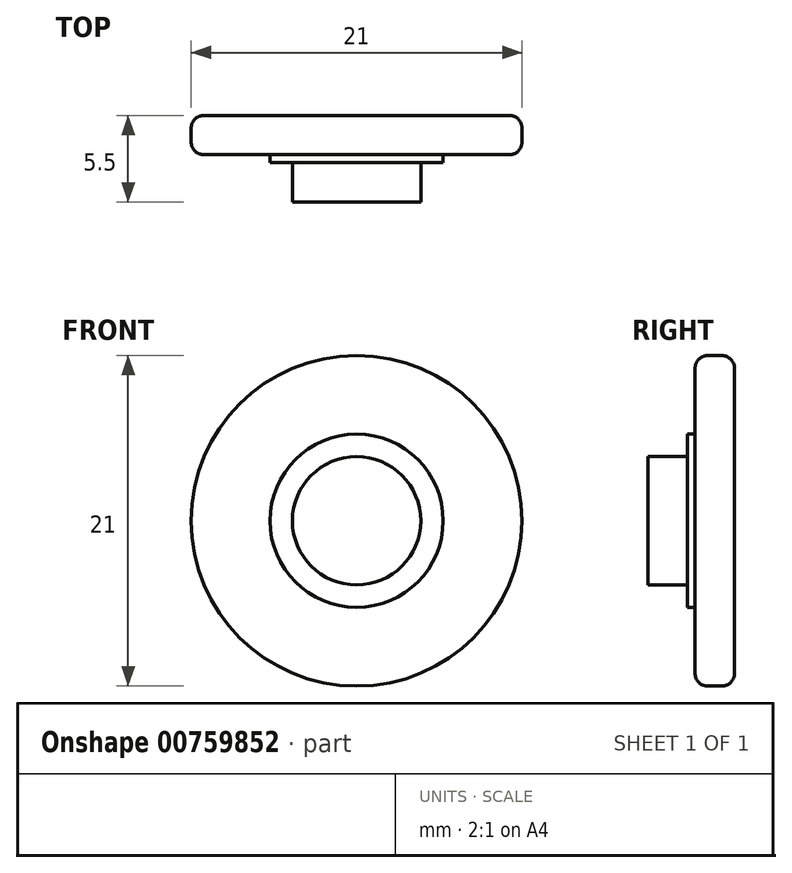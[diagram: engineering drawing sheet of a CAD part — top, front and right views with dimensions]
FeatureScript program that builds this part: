
annotation { "Feature Type Name" : "Feature", "Feature Type Description" : "" }
export const myFeature = defineFeature(function(context is Context, id is Id, definition is map)
    precondition{}
    {
        {
            var Q0;
            Q0=qCreatedBy(makeId("Front.planeOp"),FACE);
            var sketch = newSketch(context, id + "F0", { "sketchPlane" : qUnion([Q0])});
            skCircle(sketch, "E0", {"center": v(0, 0) * mm, "radius": 10.5 * mm});
            skCircle(sketch, "E1", {"center": v(0, 0) * mm, "radius": 5.5 * mm});
            skCircle(sketch, "E2", {"center": v(0, 0) * mm, "radius": 4.08 * mm});
            skSolve(sketch);
        }
        {
            var Q0;
            Q0=makeQuery(id+"F0.imprint","IMPRINT",FACE,{"disambiguationData":[TD([[makeQuery(id+"F0.imprint","IMPRINT",EDGE,{"derivedFrom":sQuery(id+"F0.wireOp",EDGE,"E1")}),1.0]])]});
            var sketch = newSketch(context, id + "F1", { "sketchPlane" : qUnion([Q0])});
            skSolve(sketch);
        }
        {
            var Q0;
            Q0 = qSketchRegion(id + "F0", true);
            var Q1;
            Q1 = qSketchRegion(id + "F1", true);
            extrude(context, id + "F2", {"entities" : qUnion([Q0, Q1]), "depth" : 2.5 * mm, "offsetDistance" : 25 * mm});
        }
        {
            var Q0;
            Q0=makeQuery(id+"F1.imprint","IMPRINT",FACE,{"disambiguationData":[TD([[makeQuery(id+"F1.imprint","IMPRINT",EDGE,{"derivedFrom":makeQuery(id+"F0.imprint","IMPRINT",EDGE,{"derivedFrom":sQuery(id+"F0.wireOp",EDGE,"E1")})}),1.0]])]});
            extrude(context, id + "F3", {"entities" : qUnion([Q0]), "operationType" : NewBodyOperationType.ADD, "depth" : 3 * mm, "offsetDistance" : 25 * mm});
        }
        {
            var Q0;
            Q0=makeQuery(id+"F1.imprint","IMPRINT",FACE,{"disambiguationData":[TD([[makeQuery(id+"F1.imprint","IMPRINT",EDGE,{"derivedFrom":makeQuery(id+"F0.imprint","IMPRINT",EDGE,{"derivedFrom":sQuery(id+"F0.wireOp",EDGE,"E2")})}),1.0]])]});
            extrude(context, id + "F4", {"entities" : qUnion([Q0]), "operationType" : NewBodyOperationType.ADD, "depth" : 5.5 * mm, "offsetDistance" : 25 * mm});
        }
        {
            var Q0;
            Q0=makeQuery(id+"F2.opExtrude","CAP_EDGE",EDGE,{"disambiguationData":[OSD([sQuery(id+"F0.wireOp",EDGE,"E0")])],"isStart":true});
            var Q1;
            Q1=makeQuery(id+"F2.opExtrude","CAP_EDGE",EDGE,{"disambiguationData":[OSD([sQuery(id+"F0.wireOp",EDGE,"E0")])],"isStart":false});
            fillet(context, id + "F5", {"entities" : qUnion([Q0, Q1]), "radius" : .8 * mm, "tangentPropagation" : true, "allowEdgeOverflow" : false});
        }
    });
